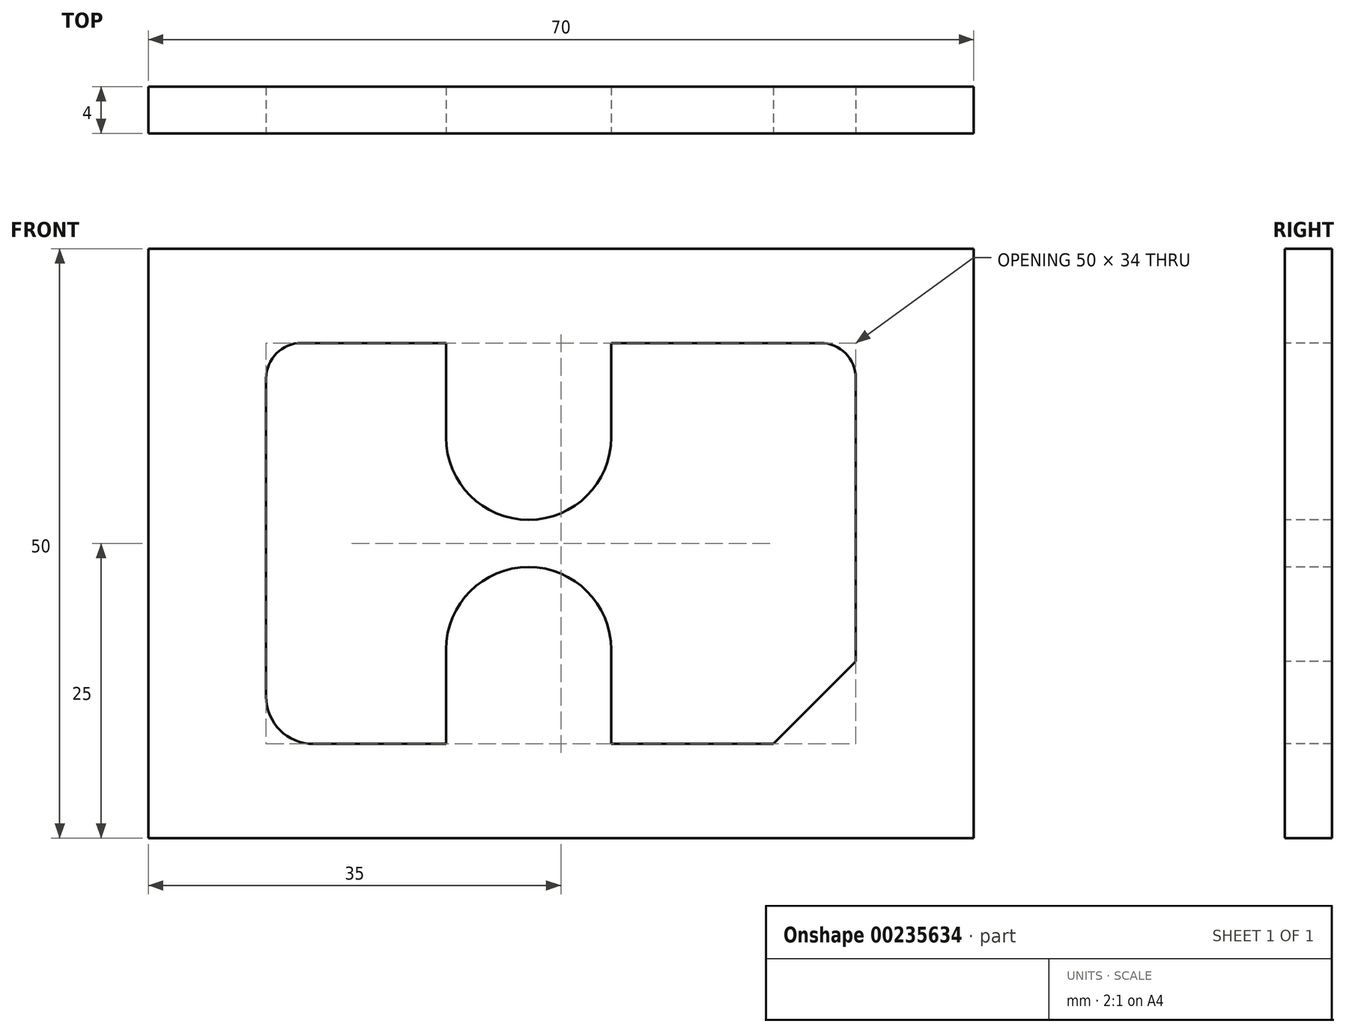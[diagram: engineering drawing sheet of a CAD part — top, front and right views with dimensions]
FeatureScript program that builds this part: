
annotation { "Feature Type Name" : "Feature", "Feature Type Description" : "" }
export const myFeature = defineFeature(function(context is Context, id is Id, definition is map)
    precondition{}
    {
        {
            var Q0;
            Q0=qCreatedBy(makeId("Front.planeOp"),FACE);
            var sketch = newSketch(context, id + "F0", { "sketchPlane" : qUnion([Q0])});
            skLineSegment(sketch, "E0.bottom", {"start": v(0, 0) * mm, "end": v(70, 0) * mm});
            skLineSegment(sketch, "E0.top", {"start": v(0, -50) * mm, "end": v(70, -50) * mm});
            skLineSegment(sketch, "E0.left", {"start": v(0, 0) * mm, "end": v(0, -50) * mm});
            skLineSegment(sketch, "E0.right", {"start": v(70, 0) * mm, "end": v(70, -50) * mm});
            skLineSegment(sketch, "E1.bottom", {"start": v(13, -8) * mm, "end": v(25.25, -8) * mm});
            skLineSegment(sketch, "E1.top", {"start": v(14, -42) * mm, "end": v(25.25, -42) * mm});
            skLineSegment(sketch, "E1.left", {"start": v(10, -11) * mm, "end": v(10, -38) * mm});
            skLineSegment(sketch, "E1.right", {"start": v(60, -11) * mm, "end": v(60, -35) * mm});
            skPoint(sketch, "E2.visualSharp", {"position": v(10, -8) * mm});
            skArc(sketch, "E2.filletArc", {"start": v(13, -8) * mm, "mid": v(10.88, -8.88) * mm, "end": v(10, -11) * mm});
            skPoint(sketch, "E3.visualSharp", {"position": v(10, -42) * mm});
            skArc(sketch, "E3.filletArc", {"start": v(10, -38) * mm, "mid": v(11.17, -40.83) * mm, "end": v(14, -42) * mm});
            skPoint(sketch, "E4.visualSharp", {"position": v(60, -8) * mm});
            skArc(sketch, "E4.filletArc", {"start": v(60, -11) * mm, "mid": v(59.12, -8.88) * mm, "end": v(57, -8) * mm});
            skLineSegment(sketch, "E5", {"start": v(60, -35) * mm, "end": v(53, -42) * mm});
            skPoint(sketch, "E6.orphan", {"position": v(60, -42) * mm});
            skLineSegment(sketch, "E7", {"start": v(25.25, -8) * mm, "end": v(25.25, -16) * mm});
            skLineSegment(sketch, "E8", {"start": v(39.25, -8) * mm, "end": v(39.25, -16) * mm});
            skLineSegment(sketch, "E9", {"start": v(39.25, -25) * mm, "end": v(40.87, -25) * mm});
            skPoint(sketch, "E9.endSnap0", {"position": v(39.25, -25) * mm});
            skPoint(sketch, "E10.orphan", {"position": v(25.25, -25) * mm});
            skLineSegment(sketch, "E11.trimOffspring", {"start": v(39.25, -8) * mm, "end": v(57, -8) * mm});
            skArc(sketch, "E12", {"start": v(25.25, -16) * mm, "mid": v(32.25, -23) * mm, "end": v(39.25, -16) * mm});
            skArc(sketch, "E13", {"start": v(39.25, -34) * mm, "mid": v(32.25, -27) * mm, "end": v(25.25, -34) * mm});
            skLineSegment(sketch, "E14.trimOffspring", {"start": v(25.25, -34) * mm, "end": v(25.25, -42) * mm});
            skLineSegment(sketch, "E15.trimOffspring", {"start": v(39.25, -34) * mm, "end": v(39.25, -42) * mm});
            skLineSegment(sketch, "E16.trimOffspring", {"start": v(39.25, -42) * mm, "end": v(53, -42) * mm});
            skSolve(sketch);
        }
        {
            var Q0;
            Q0=makeQuery(id+"F0.imprint","IMPRINT",FACE,{"disambiguationData":[TD([[makeQuery(id+"F0.imprint","IMPRINT",EDGE,{"derivedFrom":sQuery(id+"F0.wireOp",EDGE,"E0.bottom")}),-1.0]])]});
            extrude(context, id + "F1", {"entities" : qUnion([Q0]), "oppositeDirection" : true, "depth" : 4 * mm});
        }
    });
